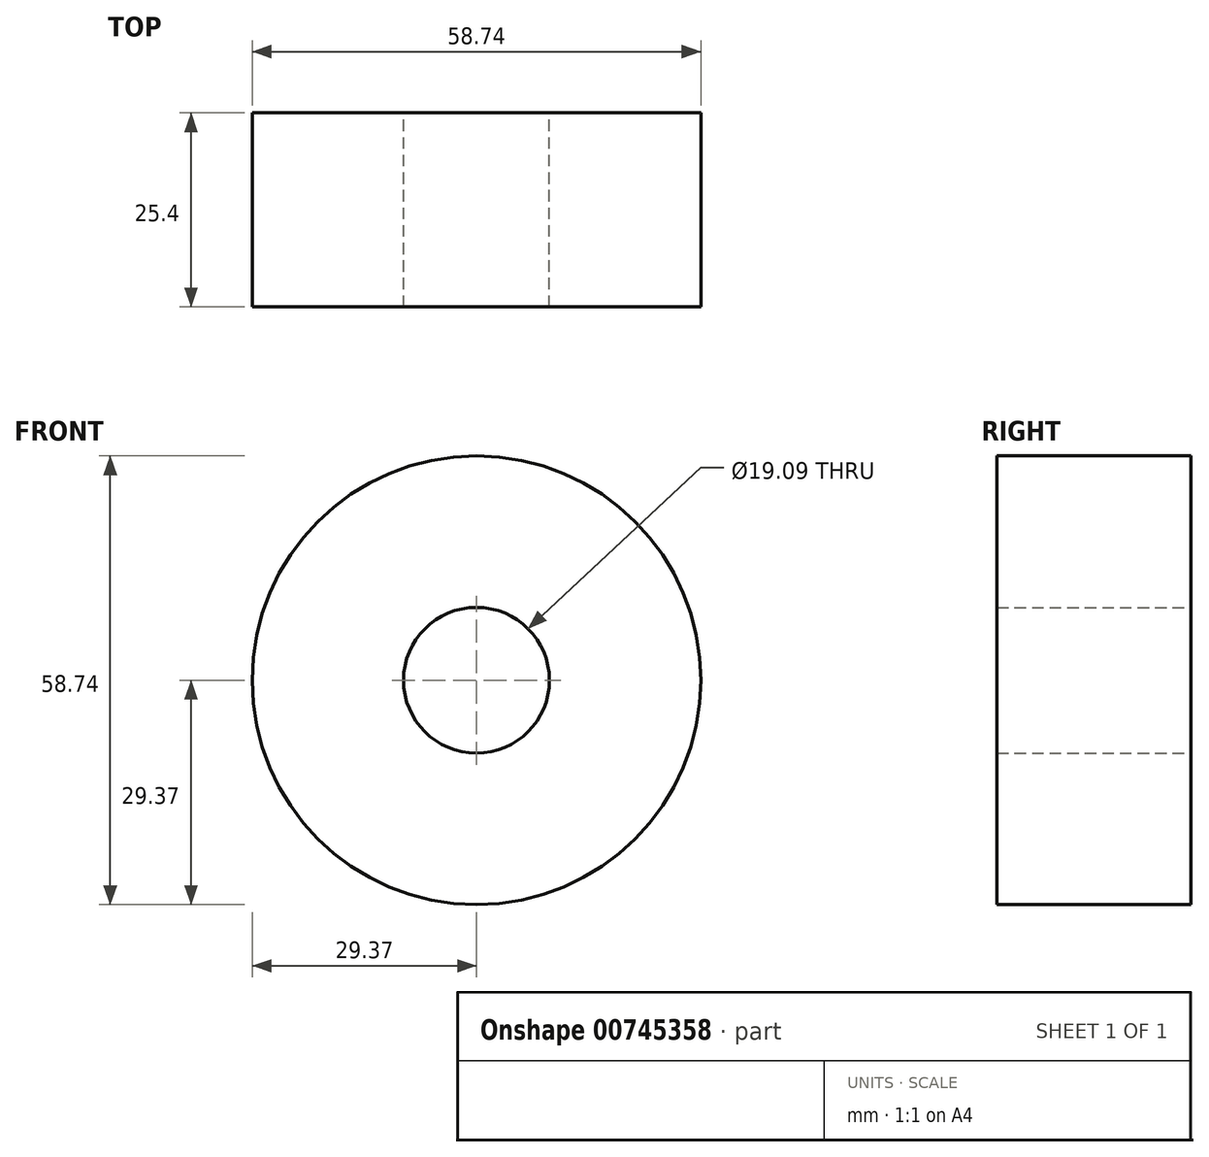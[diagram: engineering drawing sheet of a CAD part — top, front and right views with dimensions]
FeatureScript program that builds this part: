
annotation { "Feature Type Name" : "Feature", "Feature Type Description" : "" }
export const myFeature = defineFeature(function(context is Context, id is Id, definition is map)
    precondition{}
    {
        {
            var Q0;
            Q0=qCreatedBy(makeId("Front.planeOp"),FACE);
            var sketch = newSketch(context, id + "F0", { "sketchPlane" : qUnion([Q0])});
            skCircle(sketch, "E0", {"center": v(0, 0) * mm, "radius": 29.37 * mm});
            skCircle(sketch, "E1", {"center": v(0, 0) * mm, "radius": 9.55 * mm});
            skSolve(sketch);
        }
        {
            var Q0;
            Q0=makeQuery(id+"F0.imprint","IMPRINT",FACE,{"disambiguationData":[TD([[makeQuery(id+"F0.imprint","IMPRINT",EDGE,{"derivedFrom":sQuery(id+"F0.wireOp",EDGE,"E0")}),1.0]])]});
            extrude(context, id + "F1", {"entities" : qUnion([Q0]), "depth" : 25.4 * mm, "offsetDistance" : 25.4 * mm});
        }
    });
